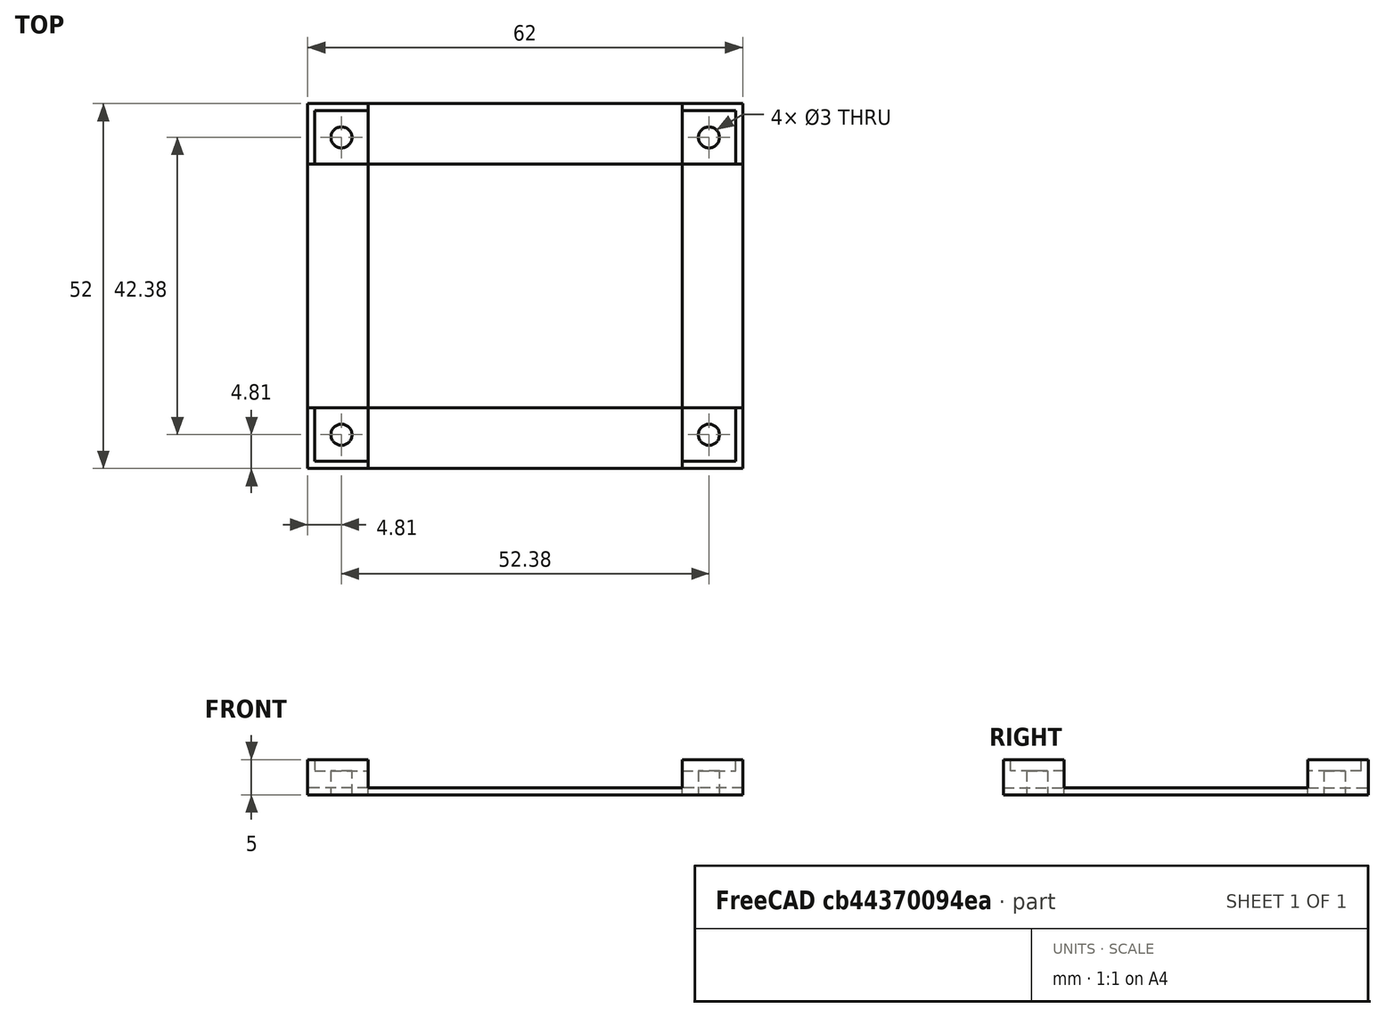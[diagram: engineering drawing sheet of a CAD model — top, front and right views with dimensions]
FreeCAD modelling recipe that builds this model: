
FCSTD DOCUMENT  (FreeCAD 0.21R33668 +26 (Git))
Label: pcb_bracket_50x60
License: All rights reserved
LicenseURL: https://en.wikipedia.org/wiki/All_rights_reserved
objects: Part::Box×7, Part::Cylinder×4, Part::MultiFuse×2, Part::Cut×1
note: 14 computed .brp shape members not serialized (recipe doc carries the construction recipe); baked Part::Feature solids carry a one-line shape summary decoded from their .brp

FEATURE [Part::Box] floor
  AttacherType = Attacher::AttachEngine3D
  Height = 1
  Length = 62
  Width = 52
FEATURE [Part::Box] floor_cut
  AttacherType = Attacher::AttachEngine3D
  Height = 1
  Length = 44.76
  Placement = pos=(8.62,8.62,0) rot=(0,0,1;0rad)
  Width = 34.76
FEATURE [Part::Box] pcb
  AttacherType = Attacher::AttachEngine3D
  Height = 1.6
  Length = 60
  Placement = pos=(1,1,3.4) rot=(0,0,1;0rad)
  Width = 50
FEATURE [Part::Box] block_0
  AttacherType = Attacher::AttachEngine3D
  Height = 5
  Length = 8.62
  Width = 8.62
FEATURE [Part::Cylinder] hole_0
  Angle = 360
  AttacherType = Attacher::AttachEngine3D
  FirstAngle = 0
  Height = 5
  Placement = pos=(4.81,4.81,0) rot=(0,0,1;0rad)
  Radius = 1.5
  SecondAngle = 0
FEATURE [Part::Box] block_1
  AttacherType = Attacher::AttachEngine3D
  Height = 5
  Length = 8.62
  Placement = pos=(0,43.38,0) rot=(0,0,1;0rad)
  Width = 8.62
FEATURE [Part::Cylinder] hole_1
  Angle = 360
  AttacherType = Attacher::AttachEngine3D
  FirstAngle = 0
  Height = 5
  Placement = pos=(4.81,47.19,0) rot=(0,0,1;0rad)
  Radius = 1.5
  SecondAngle = 0
FEATURE [Part::Box] block_2
  AttacherType = Attacher::AttachEngine3D
  Height = 5
  Length = 8.62
  Placement = pos=(53.38,0,0) rot=(0,0,1;0rad)
  Width = 8.62
FEATURE [Part::Cylinder] hole_2
  Angle = 360
  AttacherType = Attacher::AttachEngine3D
  FirstAngle = 0
  Height = 5
  Placement = pos=(57.19,4.81,0) rot=(0,0,1;0rad)
  Radius = 1.5
  SecondAngle = 0
FEATURE [Part::Box] block_3
  AttacherType = Attacher::AttachEngine3D
  Height = 5
  Length = 8.62
  Placement = pos=(53.38,43.38,0) rot=(0,0,1;0rad)
  Width = 8.62
FEATURE [Part::Cylinder] hole_3
  Angle = 360
  AttacherType = Attacher::AttachEngine3D
  FirstAngle = 0
  Height = 5
  Placement = pos=(57.19,47.19,0) rot=(0,0,1;0rad)
  Radius = 1.5
  SecondAngle = 0
FEATURE [Part::MultiFuse] base
  Shapes = -> [floor,block_0,block_1,block_2,block_3]
FEATURE [Part::MultiFuse] tool
  Shapes = -> [floor_cut,pcb,hole_0,hole_1,hole_2,hole_3]
FEATURE [Part::Cut] final
  Base = -> base
  Tool = -> tool
